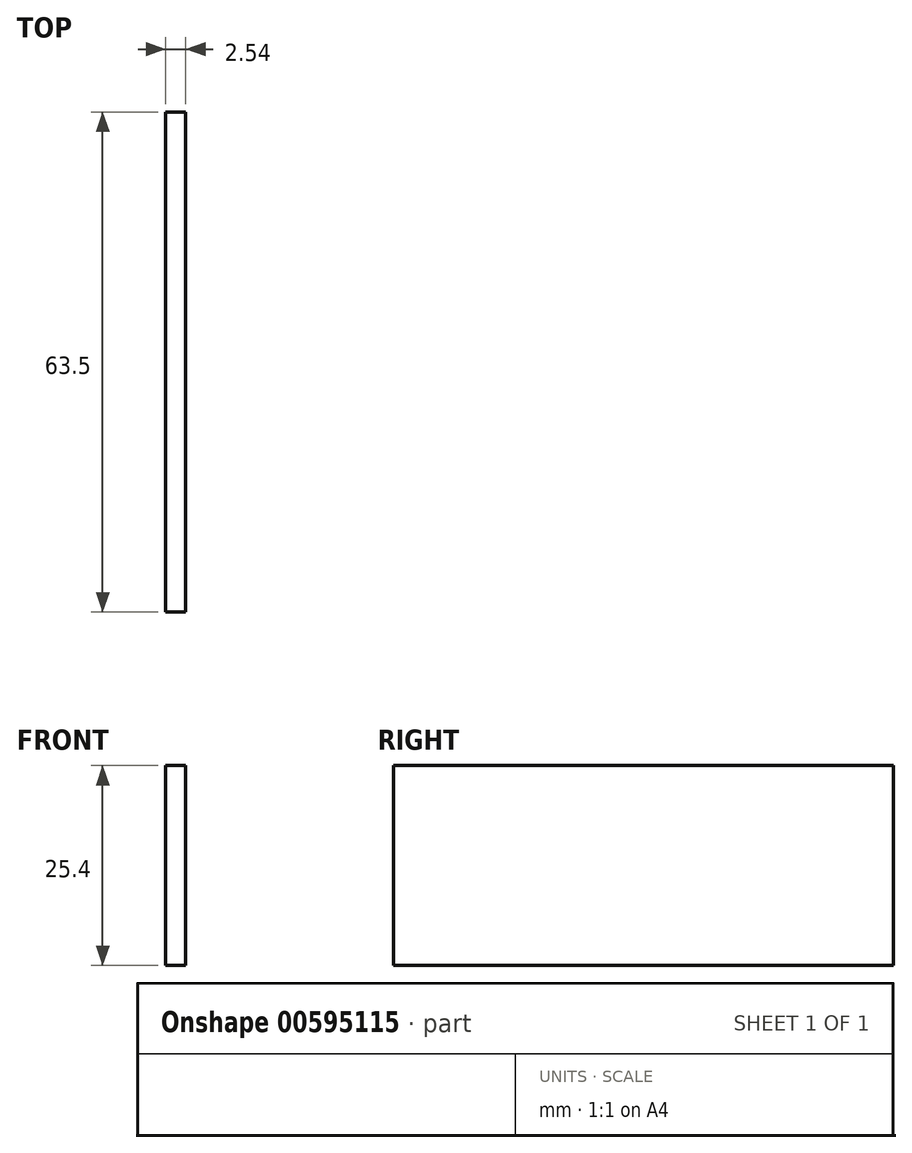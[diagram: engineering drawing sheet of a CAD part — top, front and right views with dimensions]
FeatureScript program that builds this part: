
annotation { "Feature Type Name" : "Feature", "Feature Type Description" : "" }
export const myFeature = defineFeature(function(context is Context, id is Id, definition is map)
    precondition{}
    {
        {
            var Q0;
            Q0=qCreatedBy(makeId("Top.planeOp"),FACE);
            var sketch = newSketch(context, id + "F0", { "sketchPlane" : qUnion([Q0])});
            skLineSegment(sketch, "E0.bottom", {"start": v(-51.76, 24.23) * mm, "end": v(-49.22, 24.23) * mm});
            skLineSegment(sketch, "E0.top", {"start": v(-51.76, -39.27) * mm, "end": v(-49.22, -39.27) * mm});
            skLineSegment(sketch, "E0.left", {"start": v(-51.76, 24.23) * mm, "end": v(-51.76, -39.27) * mm});
            skLineSegment(sketch, "E0.right", {"start": v(-49.22, 24.23) * mm, "end": v(-49.22, -39.27) * mm});
            skSolve(sketch);
        }
        {
            var Q0;
            Q0=makeQuery(id+"F0.imprint","IMPRINT",FACE,{"disambiguationData":[TD([[makeQuery(id+"F0.imprint","IMPRINT",EDGE,{"derivedFrom":sQuery(id+"F0.wireOp",EDGE,"E0.bottom")}),-1.0]])]});
            extrude(context, id + "F1", {"entities" : qUnion([Q0]), "depth" : 25.4 * mm, "offsetDistance" : 25.4 * mm});
        }
    });
